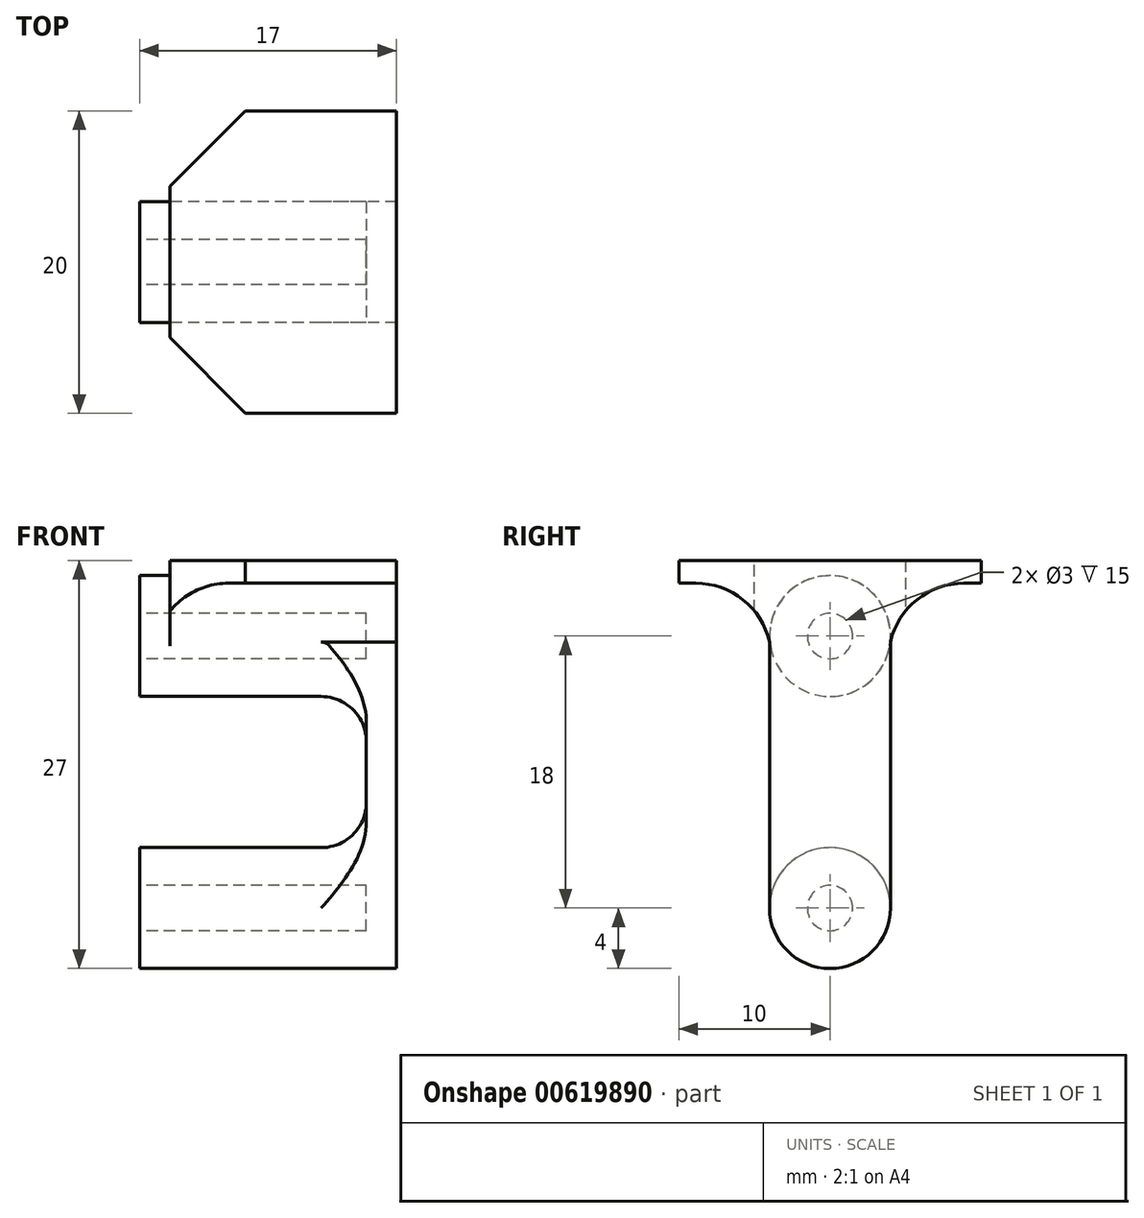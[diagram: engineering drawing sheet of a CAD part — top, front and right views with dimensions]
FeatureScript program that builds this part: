
annotation { "Feature Type Name" : "Feature", "Feature Type Description" : "" }
export const myFeature = defineFeature(function(context is Context, id is Id, definition is map)
    precondition{}
    {
        {
            var Q0;
            Q0=qCreatedBy(makeId("Right.planeOp"),FACE);
            var sketch = newSketch(context, id + "F0", { "sketchPlane" : qUnion([Q0])});
            skCircle(sketch, "E0", {"center": v(0, 0) * mm, "radius": 1.5 * mm});
            skCircle(sketch, "E1", {"center": v(0, 0) * mm, "radius": 4 * mm});
            skLineSegment(sketch, "E2", {"start": v(0, 0) * mm, "end": v(0, -18) * mm, "construction": true});
            skCircle(sketch, "E3", {"center": v(0, -18) * mm, "radius": 1.5 * mm});
            skCircle(sketch, "E4", {"center": v(0, -18) * mm, "radius": 4 * mm});
            skSolve(sketch);
        }
        {
            var Q0;
            Q0=makeQuery(id+"F0.imprint","IMPRINT",FACE,{"disambiguationData":[TD([[makeQuery(id+"F0.imprint","IMPRINT",EDGE,{"derivedFrom":sQuery(id+"F0.wireOp",EDGE,"E0")}),-1.0]])]});
            var Q1;
            Q1=makeQuery(id+"F0.imprint","IMPRINT",FACE,{"disambiguationData":[TD([[makeQuery(id+"F0.imprint","IMPRINT",EDGE,{"derivedFrom":sQuery(id+"F0.wireOp",EDGE,"E3")}),-1.0]])]});
            var Q2;
            Q2=qConstructionFilter(qBodyType(qCreatedBy(id+"F0",EDGE),BodyType.WIRE),ConstructionObject.NO);
            extrude(context, id + "F1", {"entities" : qUnion([Q0, Q1]), "surfaceEntities" : qUnion([Q2]), "depth" : 15 * mm, "offsetDistance" : 25 * mm});
        }
        {
            var Q0;
            Q0=makeQuery(id+"F1.opExtrude","CAP_FACE",FACE,{"disambiguationData":[OSD([sQuery(id+"F0.wireOp",EDGE,"E0"),sQuery(id+"F0.wireOp",EDGE,"E1")])],"isStart":false});
            var sketch = newSketch(context, id + "F2", { "sketchPlane" : qUnion([Q0])});
            skArc(sketch, "E5.0", {"start": v(4, 0) * mm, "mid": v(0, 4) * mm, "end": v(-4, 0) * mm});
            skArc(sketch, "E6.0", {"start": v(-4, -18) * mm, "mid": v(0, -22) * mm, "end": v(4, -18) * mm});
            skLineSegment(sketch, "E7", {"start": v(4, 0) * mm, "end": v(4, -18) * mm});
            skLineSegment(sketch, "E8", {"start": v(-4, 0) * mm, "end": v(-4, -18) * mm});
            skSolve(sketch);
        }
        {
            var Q0;
            Q0=qSketchRegion(id+"F2",true);
            extrude(context, id + "F3", {"entities" : qUnion([Q0]), "operationType" : NewBodyOperationType.ADD, "depth" : 2 * mm, "offsetDistance" : 25 * mm});
        }
        {
            var Q0;
            Q0=qCreatedBy(makeId("Front.planeOp"),FACE);
            var sketch = newSketch(context, id + "F4", { "sketchPlane" : qUnion([Q0])});
            skLineSegment(sketch, "E9", {"start": v(2, 5) * mm, "end": v(17, 5) * mm});
            skLineSegment(sketch, "E10", {"start": v(2, 5) * mm, "end": v(2, 3.5) * mm});
            skLineSegment(sketch, "E11", {"start": v(2, 3.5) * mm, "end": v(17, 3.5) * mm});
            skLineSegment(sketch, "E12", {"start": v(17, 5) * mm, "end": v(17, 3.5) * mm});
            skSolve(sketch);
        }
        {
            var Q0;
            Q0=qSketchRegion(id+"F4",true);
            extrude(context, id + "F5", {"entities" : qUnion([Q0]), "operationType" : NewBodyOperationType.ADD, "endBound" : BoundingType.SYMMETRIC, "depth" : 20 * mm, "offsetDistance" : 25 * mm});
        }
        {
            var Q0;
            Q0=makeQuery(id+"F5.boolean.opBoolean","INTERSECT",EDGE,{"disambiguationData":[OD(1.0)],"derivedFrom":[makeQuery(id+"F3.boolean.opBoolean","MERGE",FACE,{"derivedFrom":[makeQuery(id+"F1.opExtrude","SWEPT_FACE",FACE,{"disambiguationData":[OSD([sQuery(id+"F0.wireOp",EDGE,"E1")])]}),makeQuery(id+"F3.opExtrude","SWEPT_FACE",FACE,{"disambiguationData":[OSD([sQuery(id+"F2.wireOp",EDGE,"E5.0")])]})]}),makeQuery(id+"F5.opExtrude","SWEPT_FACE",FACE,{"disambiguationData":[OSD([sQuery(id+"F4.wireOp",EDGE,"E11")])]})]});
            var Q1;
            Q1=makeQuery(id+"F5.boolean.opBoolean","INTERSECT",EDGE,{"disambiguationData":[OD(0.0)],"derivedFrom":[makeQuery(id+"F3.boolean.opBoolean","MERGE",FACE,{"derivedFrom":[makeQuery(id+"F1.opExtrude","SWEPT_FACE",FACE,{"disambiguationData":[OSD([sQuery(id+"F0.wireOp",EDGE,"E1")])]}),makeQuery(id+"F3.opExtrude","SWEPT_FACE",FACE,{"disambiguationData":[OSD([sQuery(id+"F2.wireOp",EDGE,"E5.0")])]})]}),makeQuery(id+"F5.opExtrude","SWEPT_FACE",FACE,{"disambiguationData":[OSD([sQuery(id+"F4.wireOp",EDGE,"E11")])]})]});
            fillet(context, id + "F6", {"entities" : qUnion([Q0, Q1]), "radius" : 5 * mm, "tangentPropagation" : true, "allowEdgeOverflow" : false});
        }
        {
            var Q0;
            Q0=makeQuery(id+"F5.opExtrude","SWEPT_FACE",FACE,{"disambiguationData":[OSD([sQuery(id+"F4.wireOp",EDGE,"E11")])]});
            var sketch = newSketch(context, id + "F7", { "sketchPlane" : qUnion([Q0])});
            skLineSegment(sketch, "E13.bottom", {"start": v(17, -1) * mm, "end": v(2, -1) * mm});
            skLineSegment(sketch, "E13.top", {"start": v(17, -2.5) * mm, "end": v(2, -2.5) * mm});
            skLineSegment(sketch, "E13.left", {"start": v(17, -1) * mm, "end": v(17, -2.5) * mm});
            skLineSegment(sketch, "E13.right", {"start": v(2, -1) * mm, "end": v(2, -2.5) * mm});
            skLineSegment(sketch, "E14", {"start": v(13.38, 0) * mm, "end": v(16.05, 0) * mm, "construction": true});
            skSolve(sketch);
        }
        {
            var Q0;
            Q0=makeQuery(id+"F5.opExtrude","CAP_EDGE",EDGE,{"disambiguationData":[OSD([sQuery(id+"F4.wireOp",EDGE,"E10")])],"isStart":true});
            var Q1;
            Q1=makeQuery(id+"F5.opExtrude","CAP_EDGE",EDGE,{"disambiguationData":[OSD([sQuery(id+"F4.wireOp",EDGE,"E10")])],"isStart":false});
            chamfer(context, id + "F8", {"entities" : qUnion([Q0, Q1]), "width" : 5 * mm, "tangentPropagation" : true});
        }
        {
            var Q0;
            Q0=makeQuery(id+"F1.opExtrude","CAP_EDGE",EDGE,{"disambiguationData":[OSD([sQuery(id+"F0.wireOp",EDGE,"E1")])],"isStart":false});
            var Q1;
            Q1=makeQuery(id+"F1.opExtrude","CAP_EDGE",EDGE,{"disambiguationData":[OSD([sQuery(id+"F0.wireOp",EDGE,"E4")])],"isStart":false});
            fillet(context, id + "F9", {"entities" : qUnion([Q0, Q1]), "radius" : 3 * mm, "tangentPropagation" : true, "allowEdgeOverflow" : false});
        }
    });
